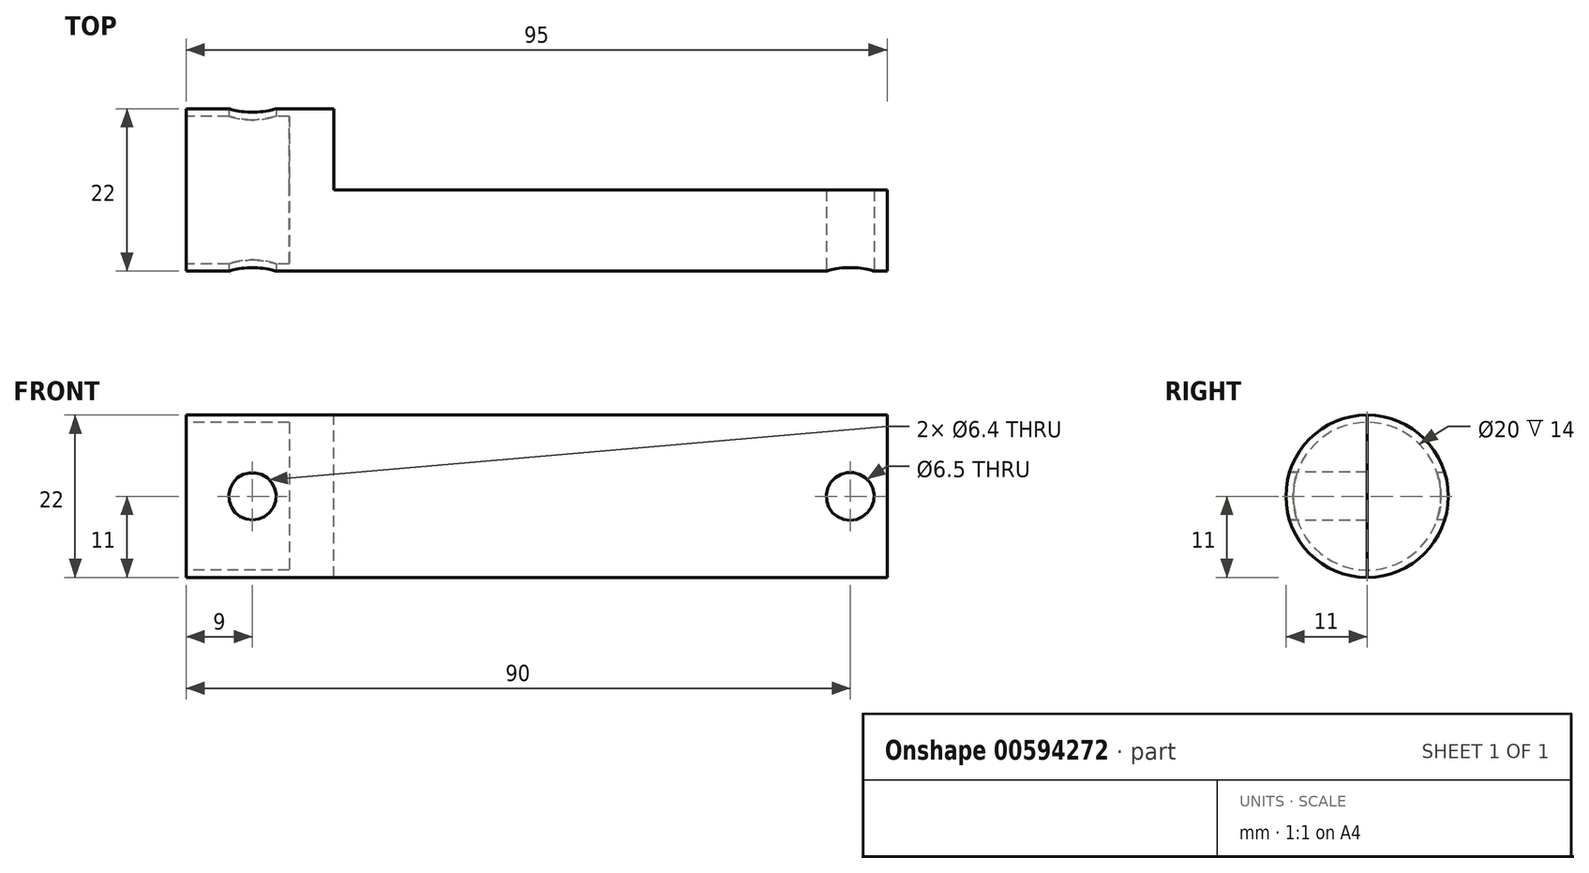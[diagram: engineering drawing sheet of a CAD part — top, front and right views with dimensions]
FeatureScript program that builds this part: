
annotation { "Feature Type Name" : "Feature", "Feature Type Description" : "" }
export const myFeature = defineFeature(function(context is Context, id is Id, definition is map)
    precondition{}
    {
        {
            var Q0;
            Q0=qCreatedBy(makeId("Right.planeOp"),FACE);
            var sketch = newSketch(context, id + "F0", { "sketchPlane" : qUnion([Q0])});
            skCircle(sketch, "E0", {"center": v(0, 0) * mm, "radius": 11 * mm});
            skSolve(sketch);
        }
        {
            var Q0;
            Q0=makeQuery(id+"F0.imprint","IMPRINT",FACE,{"disambiguationData":[TD([[makeQuery(id+"F0.imprint","IMPRINT",EDGE,{"derivedFrom":sQuery(id+"F0.wireOp",EDGE,"E0")}),1.0]])]});
            extrude(context, id + "F1", {"entities" : qUnion([Q0]), "depth" : 20 * mm, "offsetDistance" : 25 * mm});
        }
        {
            var Q0;
            Q0=makeQuery(id+"F1.opExtrude","CAP_FACE",FACE,{"disambiguationData":[OSD([sQuery(id+"F0.wireOp",EDGE,"E0")])],"isStart":true});
            var sketch = newSketch(context, id + "F2", { "sketchPlane" : qUnion([Q0])});
            skCircle(sketch, "E1", {"center": v(0, 0) * mm, "radius": 10 * mm});
            skSolve(sketch);
        }
        {
            var Q0;
            Q0=makeQuery(id+"F2.imprint","IMPRINT",FACE,{"disambiguationData":[TD([[makeQuery(id+"F2.imprint","IMPRINT",EDGE,{"derivedFrom":sQuery(id+"F2.wireOp",EDGE,"E1")}),1.0]])]});
            extrude(context, id + "F3", {"entities" : qUnion([Q0]), "operationType" : NewBodyOperationType.REMOVE, "oppositeDirection" : true, "depth" : 14 * mm, "offsetDistance" : 25 * mm});
        }
        {
            var Q0;
            Q0=makeQuery(id+"F1.opExtrude","CAP_FACE",FACE,{"disambiguationData":[OSD([sQuery(id+"F0.wireOp",EDGE,"E0")])],"isStart":false});
            var sketch = newSketch(context, id + "F4", { "sketchPlane" : qUnion([Q0])});
            skArc(sketch, "E2", {"start": v(0, 11) * mm, "mid": v(-11, 0) * mm, "end": v(0, -11) * mm});
            skLineSegment(sketch, "E3", {"start": v(0, -11) * mm, "end": v(0, 11) * mm});
            skSolve(sketch);
        }
        {
            var Q0;
            Q0 = qSketchRegion(id + "F4", true);
            extrude(context, id + "F5", {"entities" : qUnion([Q0]), "operationType" : NewBodyOperationType.ADD, "depth" : 75 * mm, "offsetDistance" : 25 * mm});
        }
        {
            var Q0;
            Q0=qCreatedBy(makeId("Front.planeOp"),FACE);
            var sketch = newSketch(context, id + "F6", { "sketchPlane" : qUnion([Q0])});
            skCircle(sketch, "E4", {"center": v(9, 0) * mm, "radius": 3.2 * mm});
            skCircle(sketch, "E5", {"center": v(90, 0) * mm, "radius": 3.25 * mm});
            skSolve(sketch);
        }
        {
            var Q0;
            Q0=makeQuery(id+"F6.imprint","IMPRINT",FACE,{"disambiguationData":[TD([[makeQuery(id+"F6.imprint","IMPRINT",EDGE,{"derivedFrom":sQuery(id+"F6.wireOp",EDGE,"E4")}),1.0]])]});
            var Q1;
            Q1=makeQuery(id+"F6.imprint","IMPRINT",FACE,{"disambiguationData":[TD([[makeQuery(id+"F6.imprint","IMPRINT",EDGE,{"derivedFrom":sQuery(id+"F6.wireOp",EDGE,"E5")}),1.0]])]});
            extrude(context, id + "F7", {"entities" : qUnion([Q0, Q1]), "operationType" : NewBodyOperationType.REMOVE, "endBound" : BoundingType.SYMMETRIC, "oppositeDirection" : true, "depth" : 25 * mm, "offsetDistance" : 25 * mm});
        }
    });
